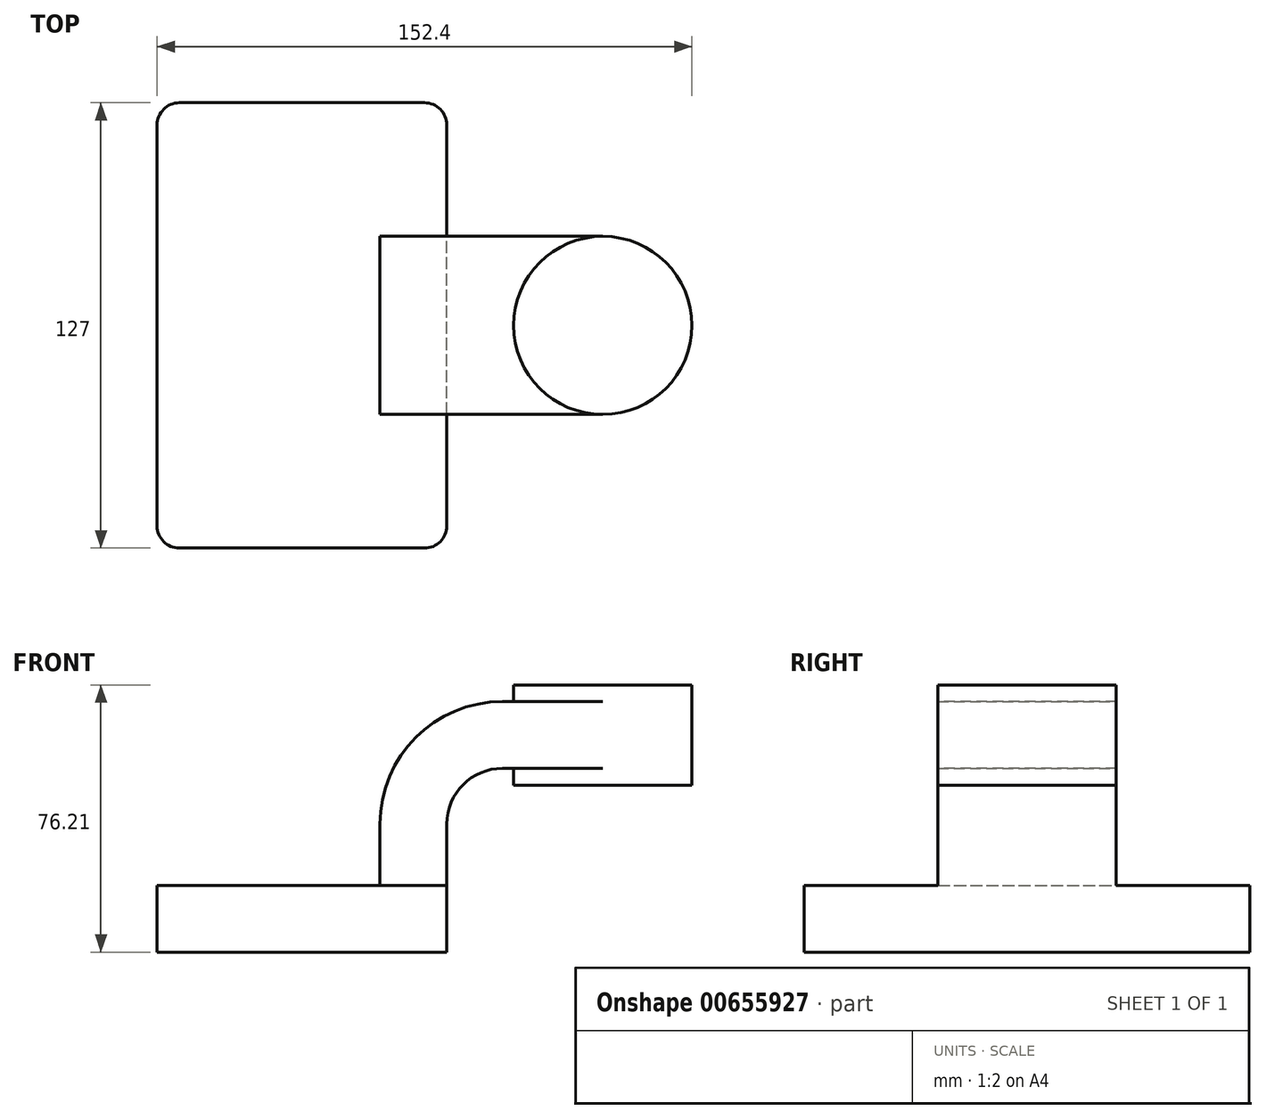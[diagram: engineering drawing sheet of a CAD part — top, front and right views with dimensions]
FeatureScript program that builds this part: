
annotation { "Feature Type Name" : "Feature", "Feature Type Description" : "" }
export const myFeature = defineFeature(function(context is Context, id is Id, definition is map)
    precondition{}
    {
        {
            var Q0;
            Q0=qCreatedBy(makeId("Front.planeOp"),FACE);
            var sketch = newSketch(context, id + "F0", { "sketchPlane" : qUnion([Q0])});
            skLineSegment(sketch, "E0.bottom", {"start": v(41.28, 9.53) * mm, "end": v(-41.28, 9.52) * mm});
            skLineSegment(sketch, "E0.top", {"start": v(41.28, -9.52) * mm, "end": v(-41.28, -9.53) * mm});
            skLineSegment(sketch, "E0.left", {"start": v(41.27, 9.53) * mm, "end": v(41.28, -9.52) * mm});
            skLineSegment(sketch, "E0.right", {"start": v(-41.28, 9.52) * mm, "end": v(-41.28, -9.53) * mm});
            skPoint(sketch, "E0.middle", {"position": v(0, 0) * mm});
            skLineSegment(sketch, "E1.bottom", {"start": v(111.12, 38.1) * mm, "end": v(60.32, 38.1) * mm});
            skLineSegment(sketch, "E1.top", {"start": v(111.12, 66.68) * mm, "end": v(60.32, 66.68) * mm});
            skLineSegment(sketch, "E1.left", {"start": v(111.12, 38.1) * mm, "end": v(111.12, 66.68) * mm});
            skLineSegment(sketch, "E1.right", {"start": v(60.32, 38.1) * mm, "end": v(60.32, 66.68) * mm});
            skPoint(sketch, "E1.middle", {"position": v(85.72, 52.39) * mm});
            skLineSegment(sketch, "E2", {"start": v(41.28, 9.53) * mm, "end": v(41.28, 9.53) * mm});
            skLineSegment(sketch, "E3", {"start": v(41.28, 9.53) * mm, "end": v(41.28, 27) * mm});
            skArc(sketch, "E4", {"start": v(41.28, 27) * mm, "mid": v(45.92, 38.23) * mm, "end": v(57.15, 42.88) * mm});
            skLineSegment(sketch, "E5", {"start": v(57.15, 42.88) * mm, "end": v(85.72, 42.88) * mm});
            skLineSegment(sketch, "E6.0", {"start": v(57.15, 61.93) * mm, "end": v(85.72, 61.93) * mm});
            skArc(sketch, "E6.1", {"start": v(22.23, 27) * mm, "mid": v(32.45, 51.7) * mm, "end": v(57.15, 61.93) * mm});
            skLineSegment(sketch, "E6.2", {"start": v(22.23, 9.53) * mm, "end": v(22.23, 27) * mm});
            skLineSegment(sketch, "E7", {"start": v(85.72, 66.68) * mm, "end": v(85.72, 38.1) * mm});
            skFitSpline(sketch, "E8", {"points": [v(-41.28, 9.52) * mm, v(57.15, 61.93) * mm], "startDerivative": vector(103.9, 126.46) * mm, "endDerivative": vector(105.25, -6.81) * mm});
            skSolve(sketch);
        }
        {
            var Q0;
            Q0=makeQuery(id+"F0.imprint","IMPRINT",FACE,{"disambiguationData":[TD([[makeQuery(id+"F0.imprint","IMPRINT",EDGE,{"derivedFrom":sQuery(id+"F0.wireOp",EDGE,"E0.top")}),-1.0]])]});
            extrude(context, id + "F1", {"entities" : qUnion([Q0]), "endBound" : BoundingType.SYMMETRIC, "depth" : 127 * mm, "offsetDistance" : 25.4 * mm});
        }
        {
            var Q0;
            {var subQ1=sQuery(id+"F0.wireOp",EDGE,"E3");Q0=makeQuery(id+"F0.imprint","IMPRINT",FACE,{"disambiguationData":[TD([[makeQuery(id+"F0.imprint","IMPRINT",EDGE,{"derivedFrom":subQ1}),1.0]])]});}
            var Q1;
            {var subQ0=sQuery(id+"F0.wireOp",EDGE,"E5");var subQ1=sQuery(id+"F0.wireOp",EDGE,"E1.right");var subQ2=makeQuery(id+"F0.imprint","INTERSECT",VERTEX,{"derivedFrom":[subQ1,subQ0]});Q1=makeQuery(id+"F0.imprint","IMPRINT",FACE,{"disambiguationData":[TD([[makeQuery(id+"F0.imprint","IMPRINT",EDGE,{"disambiguationData":[TD([[subQ2,-1.0]])],"derivedFrom":subQ1}),-1.0]])]});}
            extrude(context, id + "F2", {"entities" : qUnion([Q0, Q1]), "operationType" : NewBodyOperationType.ADD, "endBound" : BoundingType.SYMMETRIC, "depth" : 50.8 * mm, "offsetDistance" : 25.4 * mm});
        }
        {
            var Q0;
            Q0=makeQuery(id+"F0.imprint","IMPRINT",FACE,{"disambiguationData":[TD([[makeQuery(id+"F0.imprint","IMPRINT",EDGE,{"derivedFrom":sQuery(id+"F0.wireOp",EDGE,"E6.1")}),1.0]])]});
            extrude(context, id + "F3", {"entities" : qUnion([Q0]), "operationType" : NewBodyOperationType.ADD, "endBound" : BoundingType.SYMMETRIC, "depth" : 25.4 * mm, "offsetDistance" : 25.4 * mm});
        }
        {
            var Q0;
            {var subQ4=sQuery(id+"F0.wireOp",EDGE,"E1.left");Q0=makeQuery(id+"F0.imprint","IMPRINT",FACE,{"disambiguationData":[TD([[makeQuery(id+"F0.imprint","IMPRINT",EDGE,{"derivedFrom":subQ4}),1.0]])]});}
            var Q1;
            Q1=sQuery(id+"F0.wireOp",EDGE,"E7");
            revolve(context, id + "F4", {"operationType" : NewBodyOperationType.ADD, "entities" : qUnion([Q0]), "axis" : qUnion([Q1]), "revolveType" : RevolveType.FULL});
        }
        {
            var Q0;
            Q0=makeQuery(id+"F1.opExtrude","CAP_EDGE",EDGE,{"disambiguationData":[OSD([sQuery(id+"F0.wireOp",EDGE,"E0.left")])],"isStart":false});
            var Q1;
            Q1=makeQuery(id+"F1.opExtrude","CAP_EDGE",EDGE,{"disambiguationData":[OSD([sQuery(id+"F0.wireOp",EDGE,"E0.right")])],"isStart":false});
            var Q2;
            Q2=makeQuery(id+"F1.opExtrude","CAP_EDGE",EDGE,{"disambiguationData":[OSD([sQuery(id+"F0.wireOp",EDGE,"E0.left")])],"isStart":true});
            var Q3;
            Q3=makeQuery(id+"F1.opExtrude","CAP_EDGE",EDGE,{"disambiguationData":[OSD([sQuery(id+"F0.wireOp",EDGE,"E0.right")])],"isStart":true});
            fillet(context, id + "F5", {"entities" : qUnion([Q0, Q1, Q2, Q3]), "radius" : 6.35 * mm, "tangentPropagation" : true, "allowEdgeOverflow" : false});
        }
    });
